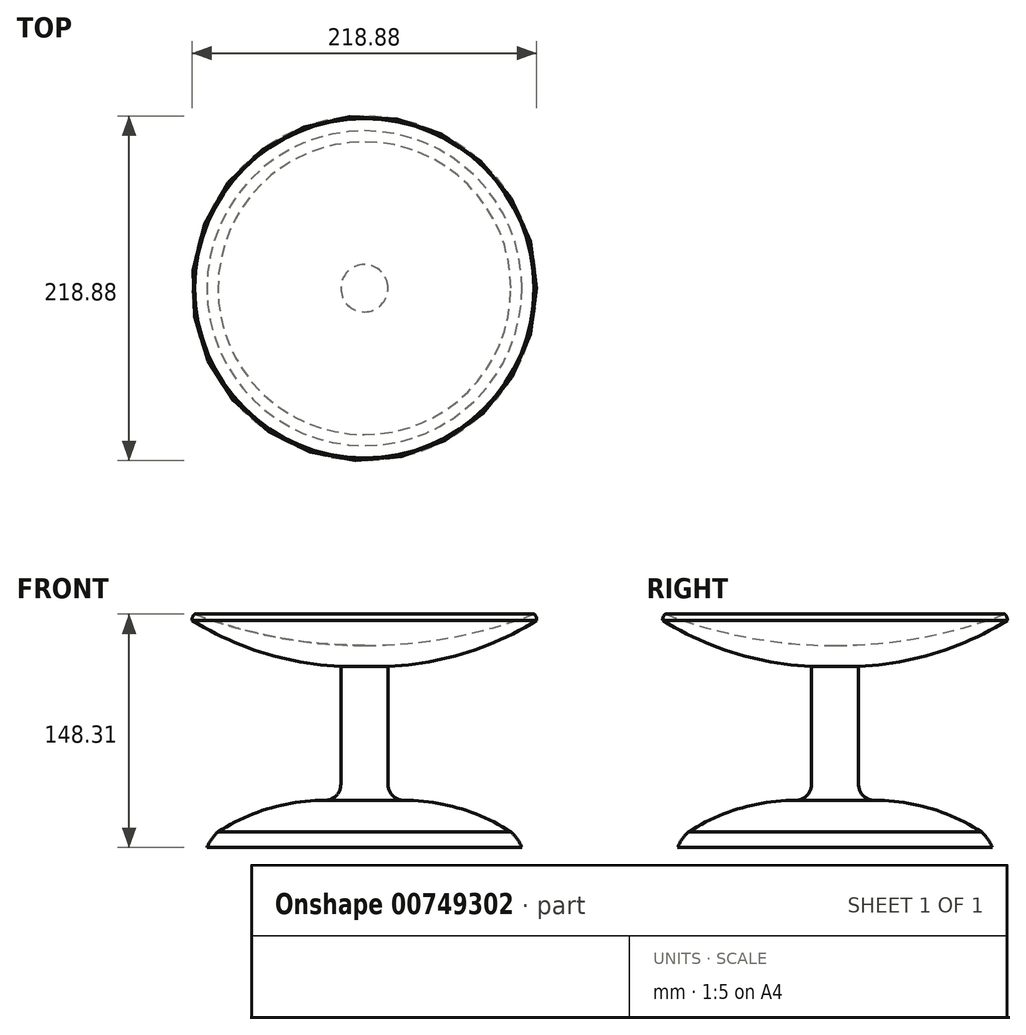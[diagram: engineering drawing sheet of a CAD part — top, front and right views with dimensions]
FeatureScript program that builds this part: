
annotation { "Feature Type Name" : "Feature", "Feature Type Description" : "" }
export const myFeature = defineFeature(function(context is Context, id is Id, definition is map)
    precondition{}
    {
        {
            var Q0;
            Q0=qCreatedBy(makeId("Front.planeOp"),FACE);
            var sketch = newSketch(context, id + "F0", { "sketchPlane" : qUnion([Q0])});
            skLineSegment(sketch, "E0", {"start": v(0, 0) * mm, "end": v(-100, 0) * mm});
            skLineSegment(sketch, "E1", {"start": v(-15, 115) * mm, "end": v(-15, 40) * mm});
            skArc(sketch, "E2", {"start": v(-25, 30) * mm, "mid": v(-60.44, 24.9) * mm, "end": v(-93, 10) * mm});
            skArc(sketch, "E3", {"start": v(-93, 10) * mm, "mid": v(-97.03, 5.37) * mm, "end": v(-100, 0) * mm});
            skPoint(sketch, "E4.visualSharp", {"position": v(-15, 29.6) * mm});
            skArc(sketch, "E4.filletArc", {"start": v(-25, 30) * mm, "mid": v(-17.93, 32.93) * mm, "end": v(-15, 40) * mm});
            skArc(sketch, "E5", {"start": v(-109.41, 144.26) * mm, "mid": v(-64.07, 123.62) * mm, "end": v(-15, 115) * mm});
            skArc(sketch, "E6", {"start": v(-107.77, 148.31) * mm, "mid": v(-54.8, 133.35) * mm, "end": v(0, 128.3) * mm});
            skLineSegment(sketch, "E7", {"start": v(0, 128.3) * mm, "end": v(22.86, 128.3) * mm, "construction": true});
            skArc(sketch, "E8", {"start": v(-107.77, 148.31) * mm, "mid": v(-109.1, 146.5) * mm, "end": v(-109.41, 144.26) * mm});
            skLineSegment(sketch, "E9", {"start": v(0, 128.3) * mm, "end": v(0, 0) * mm});
            skSolve(sketch);
        }
        {
            var Q0;
            Q0 = qSketchRegion(id + "F0", true);
            var Q1;
            Q1=sQuery(id+"F0.wireOp",EDGE,"E9");
            revolve(context, id + "F1", {"surfaceOperationType" : NewSurfaceOperationType.NEW, "entities" : qUnion([Q0]), "axis" : qUnion([Q1]), "revolveType" : RevolveType.FULL});
        }
    });
